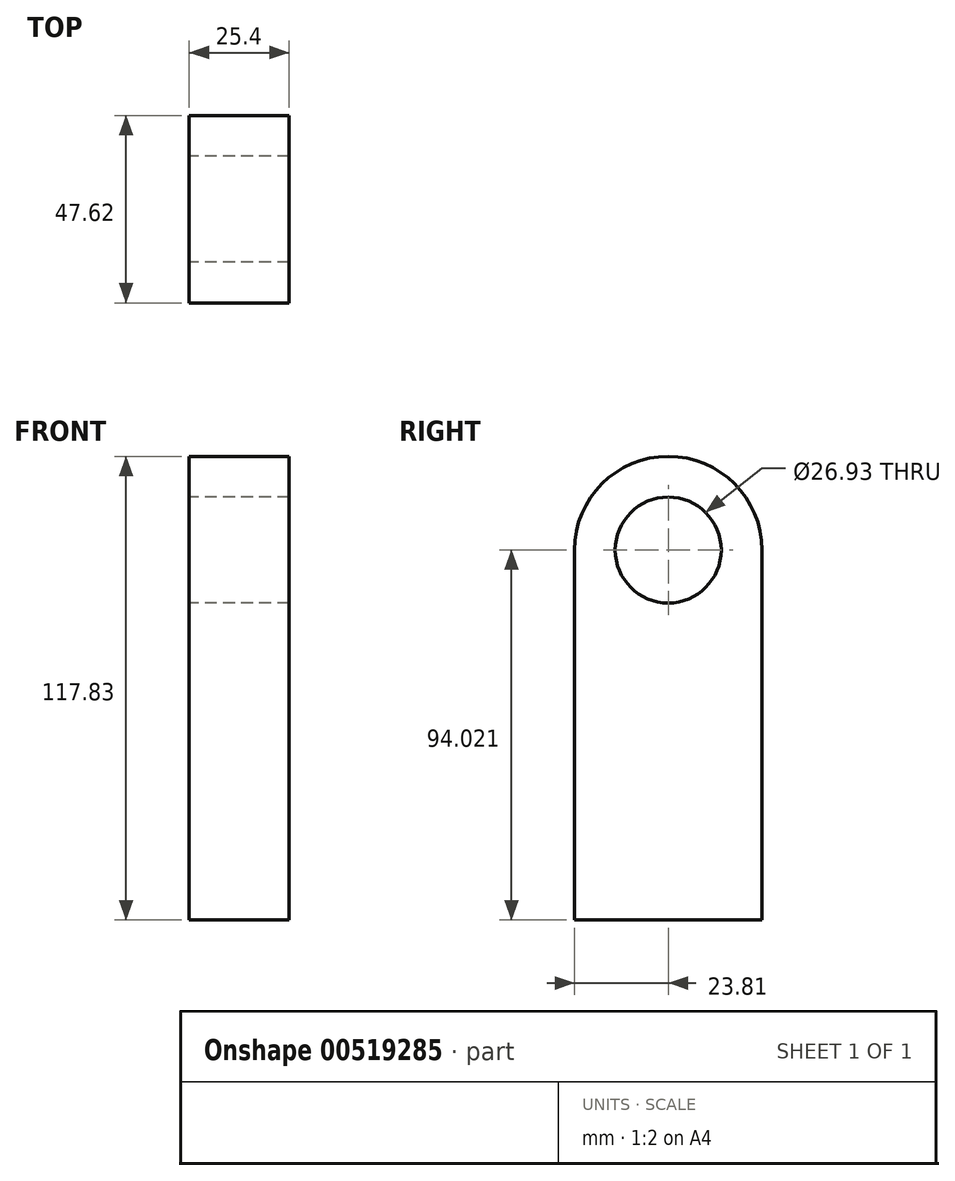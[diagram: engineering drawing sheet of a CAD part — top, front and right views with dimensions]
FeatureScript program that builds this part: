
annotation { "Feature Type Name" : "Feature", "Feature Type Description" : "" }
export const myFeature = defineFeature(function(context is Context, id is Id, definition is map)
    precondition{}
    {
        {
            var Q0;
            Q0=qCreatedBy(makeId("Right.planeOp"),FACE);
            var sketch = newSketch(context, id + "F0", { "sketchPlane" : qUnion([Q0])});
            skLineSegment(sketch, "E0.top", {"start": v(-23.81, -47.01) * mm, "end": v(23.81, -47.01) * mm});
            skLineSegment(sketch, "E0.left", {"start": v(-23.81, 47.01) * mm, "end": v(-23.81, -47.01) * mm});
            skLineSegment(sketch, "E0.right", {"start": v(23.81, 47.01) * mm, "end": v(23.81, -47.01) * mm});
            skPoint(sketch, "E0.middle", {"position": v(0, 0) * mm});
            skArc(sketch, "E1", {"start": v(23.81, 47.01) * mm, "mid": v(0, 70.82) * mm, "end": v(-23.81, 47.01) * mm});
            skCircle(sketch, "E2", {"center": v(0, 47.01) * mm, "radius": 13.46 * mm});
            skSolve(sketch);
        }
        {
            var Q0;
            Q0 = qSketchRegion(id + "F0", true);
            extrude(context, id + "F1", {"entities" : qUnion([Q0]), "depth" : 25.4 * mm, "offsetDistance" : 25.4 * mm});
        }
    });
